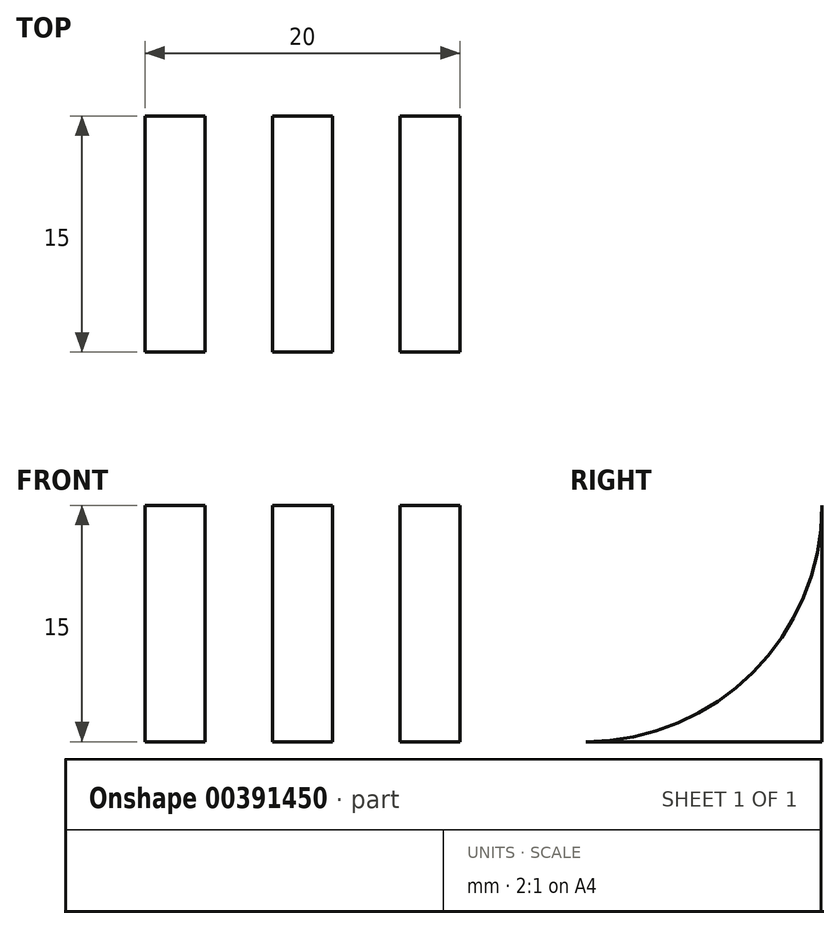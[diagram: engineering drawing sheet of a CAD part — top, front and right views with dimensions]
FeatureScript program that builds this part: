
annotation { "Feature Type Name" : "Feature", "Feature Type Description" : "" }
export const myFeature = defineFeature(function(context is Context, id is Id, definition is map)
    precondition{}
    {
        {
            var Q0;
            Q0=qCreatedBy(makeId("Front.planeOp"),FACE);
            var sketch = newSketch(context, id + "F0", { "sketchPlane" : qUnion([Q0])});
            skLineSegment(sketch, "E0.bottom", {"start": v(10, 15) * mm, "end": v(-10, 15) * mm});
            skLineSegment(sketch, "E0.top", {"start": v(10, -15) * mm, "end": v(-10, -15) * mm});
            skLineSegment(sketch, "E0.left", {"start": v(10, 15) * mm, "end": v(10, -15) * mm});
            skLineSegment(sketch, "E0.right", {"start": v(-10, 15) * mm, "end": v(-10, -15) * mm});
            skPoint(sketch, "E0.middle", {"position": v(0, 0) * mm});
            skSolve(sketch);
        }
        {
            var Q0;
            Q0 = qSketchRegion(id + "F0", true);
            extrude(context, id + "F1", {"entities" : qUnion([Q0]), "oppositeDirection" : true, "depth" : 4 * mm});
        }
        {
            var Q0;
            Q0=makeQuery(id+"F1.opExtrude","CAP_FACE",FACE,{"disambiguationData":[OSD([sQuery(id+"F0.wireOp",EDGE,"E0.bottom"),sQuery(id+"F0.wireOp",EDGE,"E0.top"),sQuery(id+"F0.wireOp",EDGE,"E0.left"),sQuery(id+"F0.wireOp",EDGE,"E0.right")])],"isStart":false});
            var sketch = newSketch(context, id + "F2", { "sketchPlane" : qUnion([Q0])});
            skLineSegment(sketch, "E1.bottom", {"start": v(-10, 15) * mm, "end": v(-6.2, 15) * mm});
            skLineSegment(sketch, "E1.top", {"start": v(-10, -15) * mm, "end": v(-6.2, -15) * mm});
            skLineSegment(sketch, "E1.left", {"start": v(-10, 15) * mm, "end": v(-10, -15) * mm});
            skLineSegment(sketch, "E1.right", {"start": v(-6.2, 15) * mm, "end": v(-6.2, -15) * mm});
            skLineSegment(sketch, "E2.bottom", {"start": v(10, 15) * mm, "end": v(6.2, 15) * mm});
            skLineSegment(sketch, "E2.top", {"start": v(10, -15) * mm, "end": v(6.2, -15) * mm});
            skLineSegment(sketch, "E2.left", {"start": v(10, 15) * mm, "end": v(10, -15) * mm});
            skLineSegment(sketch, "E2.right", {"start": v(6.2, 15) * mm, "end": v(6.2, -15) * mm});
            skLineSegment(sketch, "E3.bottom", {"start": v(-1.9, 15) * mm, "end": v(1.9, 15) * mm});
            skLineSegment(sketch, "E3.top", {"start": v(-1.9, -15) * mm, "end": v(1.9, -15) * mm});
            skLineSegment(sketch, "E3.left", {"start": v(-1.9, 15) * mm, "end": v(-1.9, -15) * mm});
            skLineSegment(sketch, "E3.right", {"start": v(1.9, 15) * mm, "end": v(1.9, -15) * mm});
            skSolve(sketch);
        }
        {
            var Q0;
            Q0 = qSketchRegion(id + "F2", true);
            extrude(context, id + "F3", {"entities" : qUnion([Q0]), "operationType" : NewBodyOperationType.ADD, "depth" : 20 * mm});
        }
        {
            var Q0;
            Q0=makeQuery(id+"F3.boolean.opBoolean","MERGE",FACE,{"derivedFrom":[makeQuery(id+"F1.opExtrude","SWEPT_FACE",FACE,{"disambiguationData":[OSD([sQuery(id+"F0.wireOp",EDGE,"E0.left")])]}),makeQuery(id+"F3.opExtrude","SWEPT_FACE",FACE,{"disambiguationData":[OSD([sQuery(id+"F2.wireOp",EDGE,"E1.left")])]})]});
            var sketch = newSketch(context, id + "F4", { "sketchPlane" : qUnion([Q0])});
            skArc(sketch, "E4", {"start": v(24, 0) * mm, "mid": v(19.6, 10.6) * mm, "end": v(9, 15) * mm});
            skArc(sketch, "E5.MirrorCS", {"start": v(24, 0) * mm, "mid": v(19.6, -10.6) * mm, "end": v(9, -15) * mm});
            skLineSegment(sketch, "E6", {"start": v(24, 0) * mm, "end": v(24, 15) * mm});
            skLineSegment(sketch, "E7", {"start": v(24, 15) * mm, "end": v(9, 15) * mm});
            skLineSegment(sketch, "E8", {"start": v(9, -15) * mm, "end": v(24, -15) * mm});
            skLineSegment(sketch, "E9", {"start": v(24, -15) * mm, "end": v(24, 0) * mm});
            skSolve(sketch);
        }
        {
            var Q0;
            Q0=makeQuery(id+"F4.imprint","IMPRINT",FACE,{"disambiguationData":[TD([[makeQuery(id+"F4.imprint","IMPRINT",EDGE,{"derivedFrom":sQuery(id+"F4.wireOp",EDGE,"E4")}),-1.0]])]});
            var Q1;
            Q1=makeQuery(id+"F4.imprint","IMPRINT",FACE,{"disambiguationData":[TD([[makeQuery(id+"F4.imprint","IMPRINT",EDGE,{"derivedFrom":sQuery(id+"F4.wireOp",EDGE,"E5.MirrorCS")}),1.0]])]});
            extrude(context, id + "F5", {"entities" : qUnion([Q0, Q1]), "operationType" : NewBodyOperationType.REMOVE, "oppositeDirection" : true, "depth" : 25 * mm});
        }
        {
            var Q0;
            Q0=makeQuery(id+"F3.boolean.opBoolean","MERGE",FACE,{"derivedFrom":[makeQuery(id+"F1.opExtrude","SWEPT_FACE",FACE,{"disambiguationData":[OSD([sQuery(id+"F0.wireOp",EDGE,"E0.left")])]}),makeQuery(id+"F3.opExtrude","SWEPT_FACE",FACE,{"disambiguationData":[OSD([sQuery(id+"F2.wireOp",EDGE,"E1.left")])]})]});
            var sketch = newSketch(context, id + "F6", { "sketchPlane" : qUnion([Q0])});
            skCircle(sketch, "E10", {"center": v(16, 0) * mm, "radius": 3 * mm});
            skSolve(sketch);
        }
        {
            var Q0;
            Q0 = qSketchRegion(id + "F6", true);
            extrude(context, id + "F7", {"entities" : qUnion([Q0]), "operationType" : NewBodyOperationType.REMOVE, "oppositeDirection" : true, "depth" : 25 * mm});
        }
    });
